# Revit family: Laundry_Faucet_with_Flexible_Spout-Elkay-LK2500_LS_CR (1)
name_source: partatom
category: Plumbing Fixtures
units: mm (PartAtom-declared; Revit-internal decimal feet)

## family parameters
Cut with Voids When Loaded = No
Host = Face
Maintain Annotation Orientation = No
OmniClass Number = 23.45.55.14
OmniClass Title = Single Faucets
Part Type = Normal
Room Calculation Point = No
Round Connector Dimension = Use Diameter
Shared = No

## types (2) — shared parameters
Activation Method = Manually Operated
Approx. Shipping Weight (lbs) = 5
CW Connection = Yes
CWFU = 1
Default Elevation = 48 "
Faucet Hole Size(min) = 1.5 "
Flow Rate (GPM) = 2 GPM
HW Connection = Yes
Handle Type = Forward Only Lever Handle
Inlet Connection Size (inch) = 0.5 "
Manufacturer = Elkay Manufacturer Company
Manufacturer Brand = Elkay (by Zurn Elkay Water Solutions)
Product Documentation Link = https://www.elkayfiles.com
Product Installation Sheet URL = https://www.elkayfiles.com
Product Page URL = https://www.elkay.com
Product Weight (lbs) = 5
Product data URL = https://bimobject.com
Repair Parts URL = https://www.elkayfiles.com
Spout Height = 14.38 "
Spout Reach = 8.38 "
Spout Type = Flexible Spout
URL = https://www.elkay.com
Vent Connection = No
Waste Connection = No
zero-valued in all types: HWFU, WFU

## per-type parameters (varying)
| type | Assembly Code | Description | Main Material | Model |
| LK2500CR (Pursuit™ Laundry/Utility Faucet with Flexible Spout) | D2010 | Pursuit™ Laundry/Utility Faucet with Flexible Spout Forward Only Lever Handle Chrome | Finish-Elkay - Chrome | LK2500CR |
| LK2500LS (Pursuit™ Laundry/Utility Faucet with Flexible Spout) | D2020300 | Pursuit™ Laundry/Utility Faucet with Flexible Spout Forward Only Lever Handle Lustrous Steel | Finish-Elkay -lustrous steel | LK2500LS |

## geometry (parser evidence)
native form markers: Sweep x7
no freeform markers — native parametric forms only
